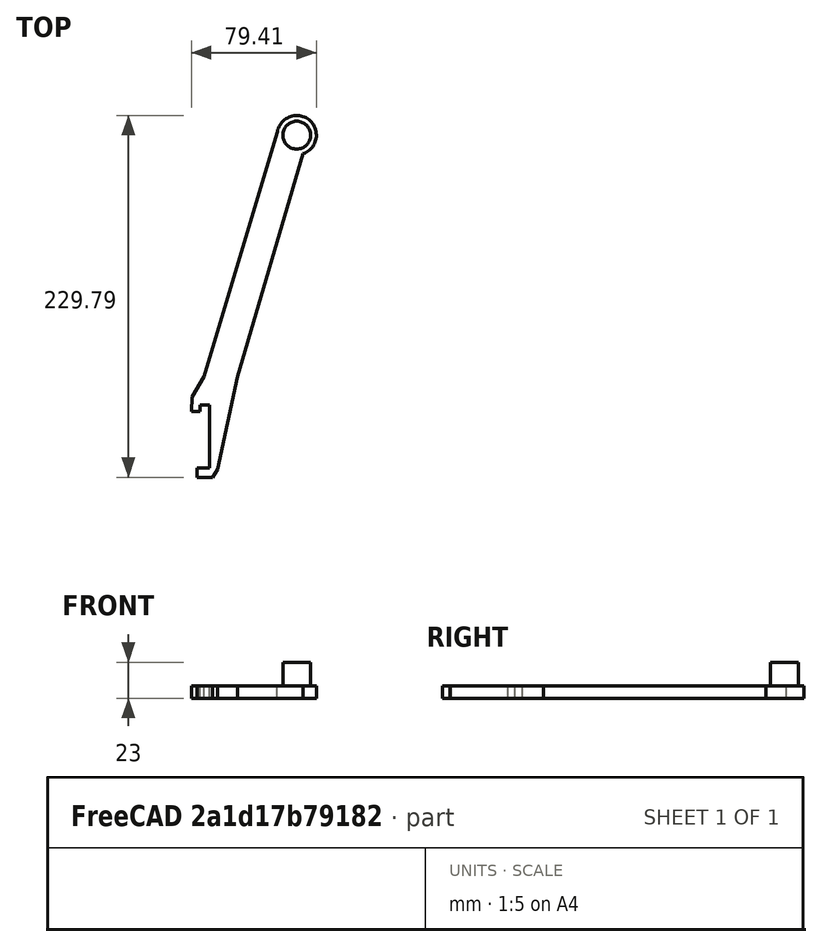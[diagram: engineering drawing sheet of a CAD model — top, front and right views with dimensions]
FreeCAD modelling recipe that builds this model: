
FCSTD DOCUMENT  (FreeCAD 0.16R6705 (Git))
Label: myholder
License: All rights reserved
LicenseURL: http://it.wikipedia.org/wiki/<copyright redacted>
objects: Sketcher::SketchObject×2, PartDesign::Pad×2
note: 6 computed .brp shape members not serialized (recipe doc carries the construction recipe); baked Part::Feature solids carry a one-line shape summary decoded from their .brp

FEATURE [Sketcher::SketchObject] Sketch015
  sketch-geometry (15):
    g0: LineSegment StartX=0 StartY=-40.1 StartZ=0 EndX=0 EndY=0 EndZ=0
    g1: LineSegment StartX=17.8486 StartY=18.1391 StartZ=0 EndX=59.4636 EndY=159.5 EndZ=0
    g2: LineSegment StartX=-8 StartY=-40.1 StartZ=0 EndX=0 EndY=-40.1 EndZ=0
    g3: LineSegment StartX=-3.48139 StartY=18.1153 StartZ=0 EndX=-11 EndY=5 EndZ=0
    g4: ArcOfCircle CenterX=55.3123 CenterY=171.291 CenterZ=0 NormalX=0 NormalY=0 NormalZ=1 Radius=12.5 StartAngle=5.05092 EndAngle=9.32583
    g5: LineSegment StartX=-8 StartY=-40.1 StartZ=0 EndX=-8 EndY=-46 EndZ=0
    g6: LineSegment StartX=-8 StartY=-46 StartZ=0 EndX=2 EndY=-46 EndZ=0
    g7: LineSegment StartX=0 StartY=0 StartZ=0 EndX=-6.2 EndY=0 EndZ=0
    g8: LineSegment StartX=-3.48139 StartY=18.1153 StartZ=0 EndX=42.8735 EndY=172.526 EndZ=0
    g9: LineSegment StartX=5 StartY=-41 StartZ=0 EndX=17.8486 EndY=18.1391 EndZ=0
    g10: LineSegment StartX=-6.2 StartY=0 StartZ=0 EndX=-6.2 EndY=-4.3 EndZ=0
    g11: LineSegment StartX=-8 StartY=-40.1 StartZ=0 EndX=0 EndY=-40.1 EndZ=0
    g12: LineSegment StartX=2 StartY=-46 StartZ=0 EndX=5 EndY=-41 EndZ=0
    g13: LineSegment StartX=-11 StartY=5 StartZ=0 EndX=-11.6 EndY=-4.3 EndZ=0
    g14: LineSegment StartX=-11.6 StartY=-4.3 StartZ=0 EndX=-6.2 EndY=-4.3 EndZ=0
  constraints (7):
    c: PointOnObject(g10,g14)
    c: Coincident(g2,g11)
    c: Radius(g4) = 12.5
    c: Distance(g1,g4) = 21.0925
    c: Coincident(g4,g1)
    c: Coincident(g8,g4)
    c: Distance(g-1,g4) = 180
FEATURE [PartDesign::Pad] Pad
  Length = 8
  Length2 = 100
  Sketch = -> Sketch015
  Type = 0
FEATURE [Sketcher::SketchObject] Sketch
  ExternalGeometry = -> [Pad]
  Placement = pos=(0,0,8) rot=(0,0,1;0rad)
  Support = -> Pad [Face16]
  sketch-geometry (1):
    g0: Circle CenterX=55.3123 CenterY=171.291 CenterZ=0 NormalX=0 NormalY=0 NormalZ=1 Radius=8.82832
  constraints (1):
    c: Coincident(g-3,g0)
FEATURE [PartDesign::Pad] Pad001
  Length = 15
  Length2 = 100
  Sketch = -> Sketch
  Type = 0
